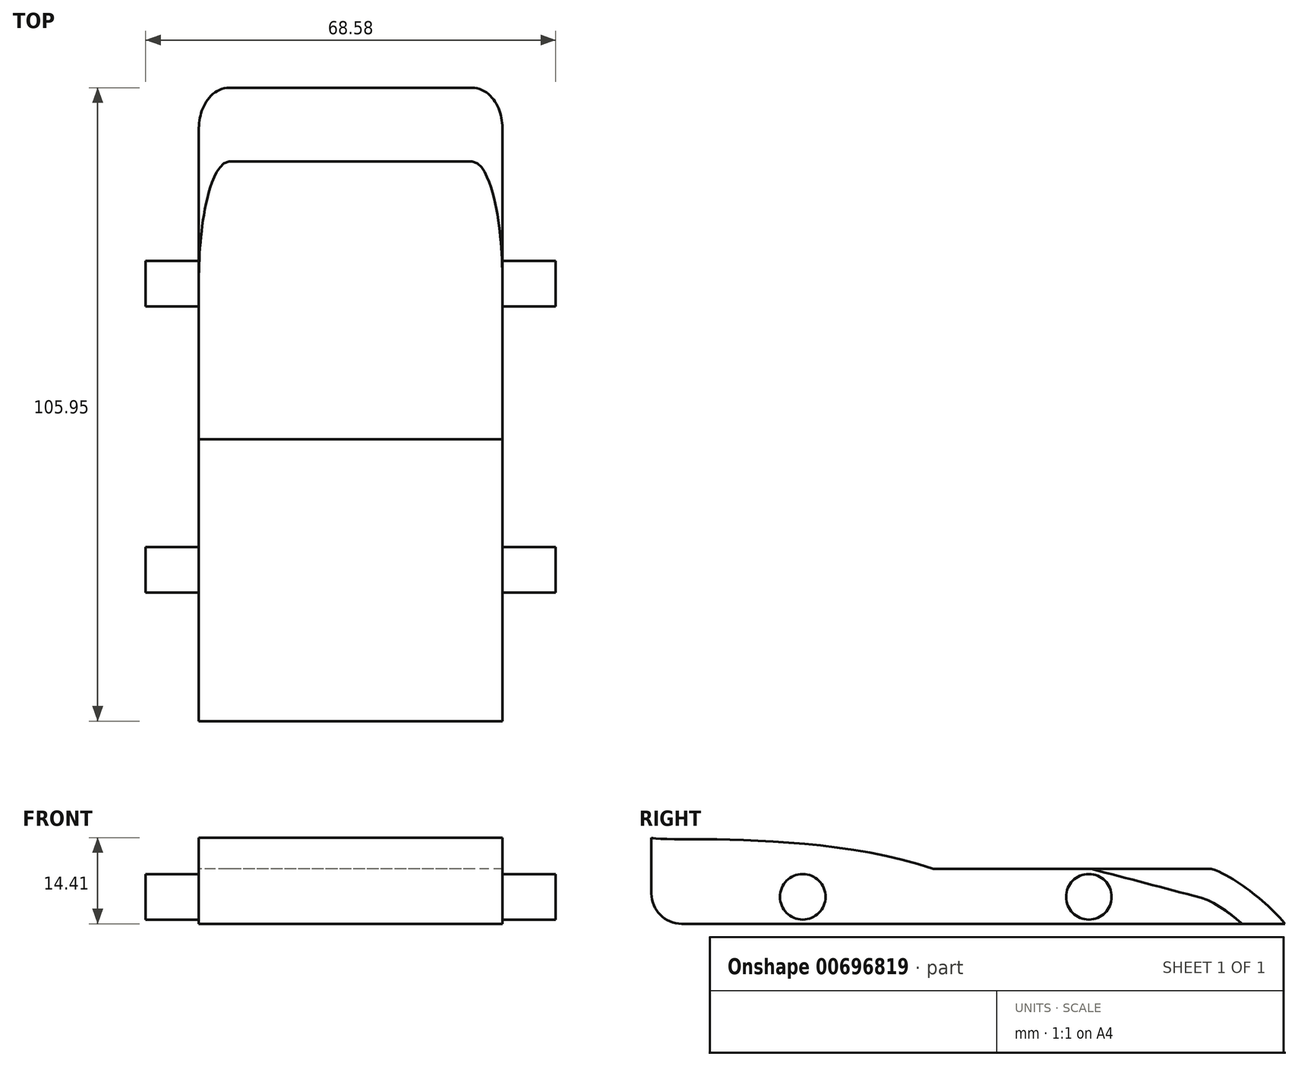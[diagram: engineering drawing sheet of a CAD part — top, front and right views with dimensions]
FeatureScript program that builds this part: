
annotation { "Feature Type Name" : "Feature", "Feature Type Description" : "" }
export const myFeature = defineFeature(function(context is Context, id is Id, definition is map)
    precondition{}
    {
        {
            var Q0;
            Q0=qCreatedBy(makeId("Right.planeOp"),FACE);
            var sketch = newSketch(context, id + "F0", { "sketchPlane" : qUnion([Q0])});
            skLineSegment(sketch, "E0.bottom", {"start": v(-59.74, 44.9) * mm, "end": v(67.26, 44.9) * mm, "construction": true});
            skLineSegment(sketch, "E0.top", {"start": v(-59.74, -31.3) * mm, "end": v(67.26, -31.3) * mm, "construction": true});
            skLineSegment(sketch, "E0.left", {"start": v(-59.74, 44.9) * mm, "end": v(-59.74, -31.3) * mm, "construction": true});
            skLineSegment(sketch, "E0.right", {"start": v(67.26, 44.9) * mm, "end": v(67.26, -31.3) * mm, "construction": true});
            skLineSegment(sketch, "E1", {"start": v(-47.15, 0) * mm, "end": v(58.8, 0) * mm});
            skLineSegment(sketch, "E2", {"start": v(-41.71, 9.17) * mm, "end": v(46.47, 9.17) * mm});
            skLineSegment(sketch, "E3", {"start": v(-47.15, 0) * mm, "end": v(-47.15, 14.4) * mm});
            skFitSpline(sketch, "E4", {"points": [v(58.8, 0) * mm, v(46.47, 9.17) * mm], "startDerivative": vector(-9.4, 11.63) * mm, "endDerivative": vector(-9.44, 2.47) * mm});
            skFitSpline(sketch, "E5", {"points": [v(-41.71, 9.17) * mm, v(-47.15, 14.4) * mm], "startDerivative": vector(-16.31, 2.36) * mm, "endDerivative": vector(-2.28, 2.61) * mm});
            skFitSpline(sketch, "E6", {"points": [v(0, 9.17) * mm, v(-47.15, 14.4) * mm], "startDerivative": vector(-57.93, 19.92) * mm, "endDerivative": vector(-2.28, 2.61) * mm});
            skSolve(sketch);
        }
        {
            var Q0;
            Q0 = qSketchRegion(id + "F0", true);
            extrude(context, id + "F1", {"entities" : qUnion([Q0]), "depth" : 50.8 * mm, "offsetDistance" : 25.4 * mm});
        }
        {
            var Q0;
            Q0=makeQuery(id+"F1.opExtrude","CAP_FACE",FACE,{"disambiguationData":[OSD([sQuery(id+"F0.wireOp",EDGE,"E1"),sQuery(id+"F0.wireOp",EDGE,"E2"),sQuery(id+"F0.wireOp",EDGE,"E3"),sQuery(id+"F0.wireOp",EDGE,"E4"),sQuery(id+"F0.wireOp",EDGE,"E5")])],"isStart":false});
            var sketch = newSketch(context, id + "F2", { "sketchPlane" : qUnion([Q0])});
            skCircle(sketch, "E7", {"center": v(-21.83, 4.5) * mm, "radius": 3.81 * mm});
            skCircle(sketch, "E8", {"center": v(26.02, 4.5) * mm, "radius": 3.81 * mm});
            skSolve(sketch);
        }
        {
            var Q0;
            Q0 = qSketchRegion(id + "F2", true);
            extrude(context, id + "F3", {"entities" : qUnion([Q0]), "operationType" : NewBodyOperationType.ADD, "depth" : 8.9 * mm, "offsetDistance" : 25.4 * mm, "hasSecondDirection" : true, "secondDirectionOppositeDirection" : true, "secondDirectionDepth" : 59.69 * mm});
        }
        {
            var Q0;
            Q0=makeQuery(id+"F1.opExtrude","SWEPT_EDGE",EDGE,{"disambiguationData":[OSD([sQuery(id+"F0.wireOp",EDGE,"E1"),sQuery(id+"F0.wireOp",EDGE,"E3")])]});
            fillet(context, id + "F4", {"entities" : qUnion([Q0]), "radius" : 5.08 * mm, "tangentPropagation" : true, "allowEdgeOverflow" : false});
        }
        {
            var Q0;
            Q0=makeQuery(id+"F1.opExtrude","CAP_EDGE",EDGE,{"disambiguationData":[OSD([sQuery(id+"F0.wireOp",EDGE,"E4")])],"isStart":false});
            var Q1;
            Q1=makeQuery(id+"F1.opExtrude","CAP_EDGE",EDGE,{"disambiguationData":[OSD([sQuery(id+"F0.wireOp",EDGE,"E4")])],"isStart":true});
            fillet(context, id + "F5", {"entities" : qUnion([Q0, Q1]), "radius" : 5.08 * mm, "tangentPropagation" : true, "allowEdgeOverflow" : false});
        }
    });
